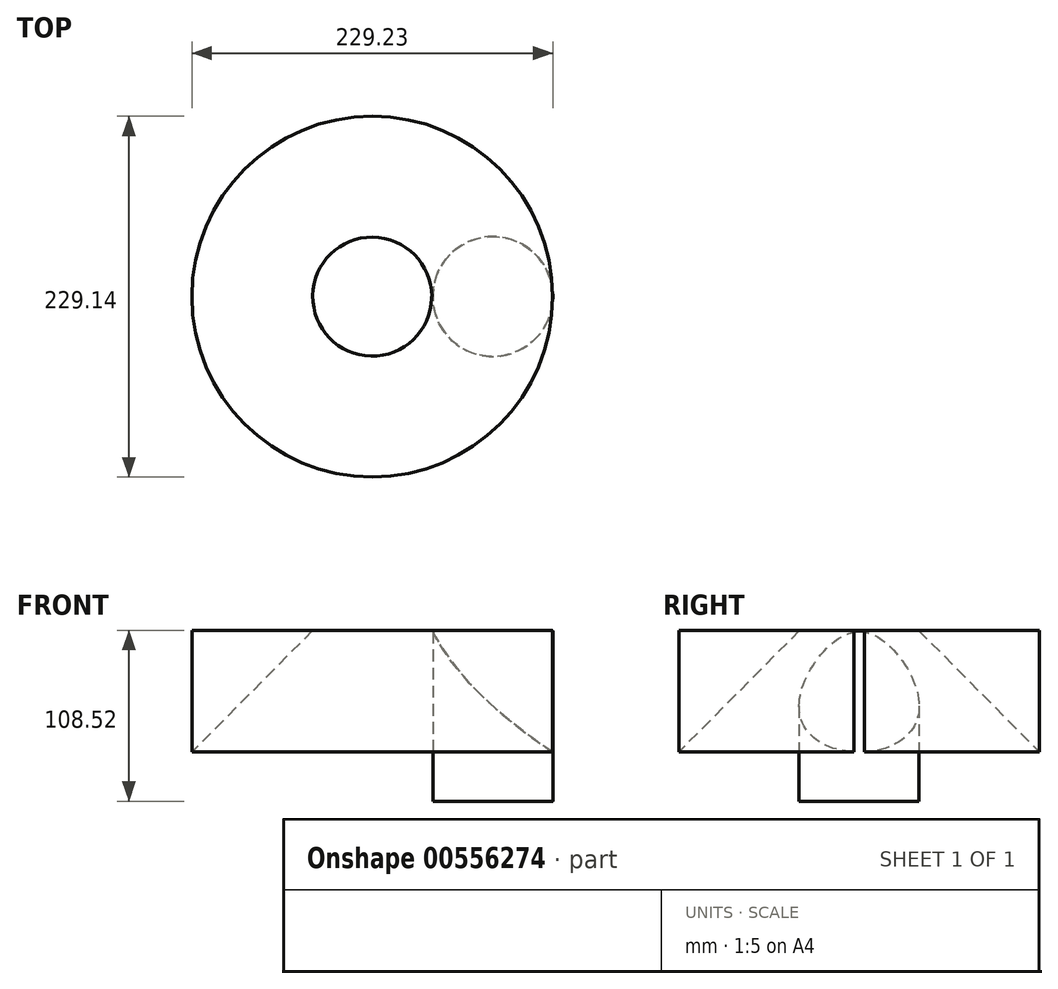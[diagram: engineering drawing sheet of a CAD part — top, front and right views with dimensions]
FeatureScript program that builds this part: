
annotation { "Feature Type Name" : "Feature", "Feature Type Description" : "" }
export const myFeature = defineFeature(function(context is Context, id is Id, definition is map)
    precondition{}
    {
        {
            var Q0;
            Q0=qCreatedBy(makeId("Top.planeOp"),FACE);
            var sketch = newSketch(context, id + "F0", { "sketchPlane" : qUnion([Q0])});
            skCircle(sketch, "E0", {"center": v(0, 0) * mm, "radius": 38.1 * mm});
            skSolve(sketch);
        }
        {
            var Q0;
            Q0=makeQuery(id+"F0.imprint","IMPRINT",FACE,{"disambiguationData":[TD([[makeQuery(id+"F0.imprint","IMPRINT",EDGE,{"derivedFrom":sQuery(id+"F0.wireOp",EDGE,"E0")}),1.0]])]});
            extrude(context, id + "F1", {"entities" : qUnion([Q0]), "depth" : 108.2 * mm, "offsetDistance" : 25.4 * mm});
        }
        {
            var Q0;
            Q0=qCreatedBy(makeId("Front.planeOp"),FACE);
            var sketch = newSketch(context, id + "F2", { "sketchPlane" : qUnion([Q0])});
            skLineSegment(sketch, "E1", {"start": v(-38.77, 108.52) * mm, "end": v(38, 108.52) * mm});
            skLineSegment(sketch, "E2", {"start": v(38, 108.52) * mm, "end": v(38, 31.26) * mm});
            skLineSegment(sketch, "E3", {"start": v(38, 31.26) * mm, "end": v(-38.77, 108.52) * mm});
            skLineSegment(sketch, "E4", {"start": v(-76.56, 60.75) * mm, "end": v(-76.56, 27.28) * mm});
            skSolve(sketch);
        }
        {
            var Q0;
            Q0=makeQuery(id+"F2.imprint","IMPRINT",FACE,{"disambiguationData":[TD([[makeQuery(id+"F2.imprint","IMPRINT",EDGE,{"derivedFrom":sQuery(id+"F2.wireOp",EDGE,"E1")}),-1.0]])]});
            var Q1;
            Q1=sQuery(id+"F2.wireOp",EDGE,"E4");
            revolve(context, id + "F3", {"operationType" : NewBodyOperationType.ADD, "entities" : qUnion([Q0]), "axis" : qUnion([Q1]), "revolveType" : RevolveType.FULL});
        }
    });
